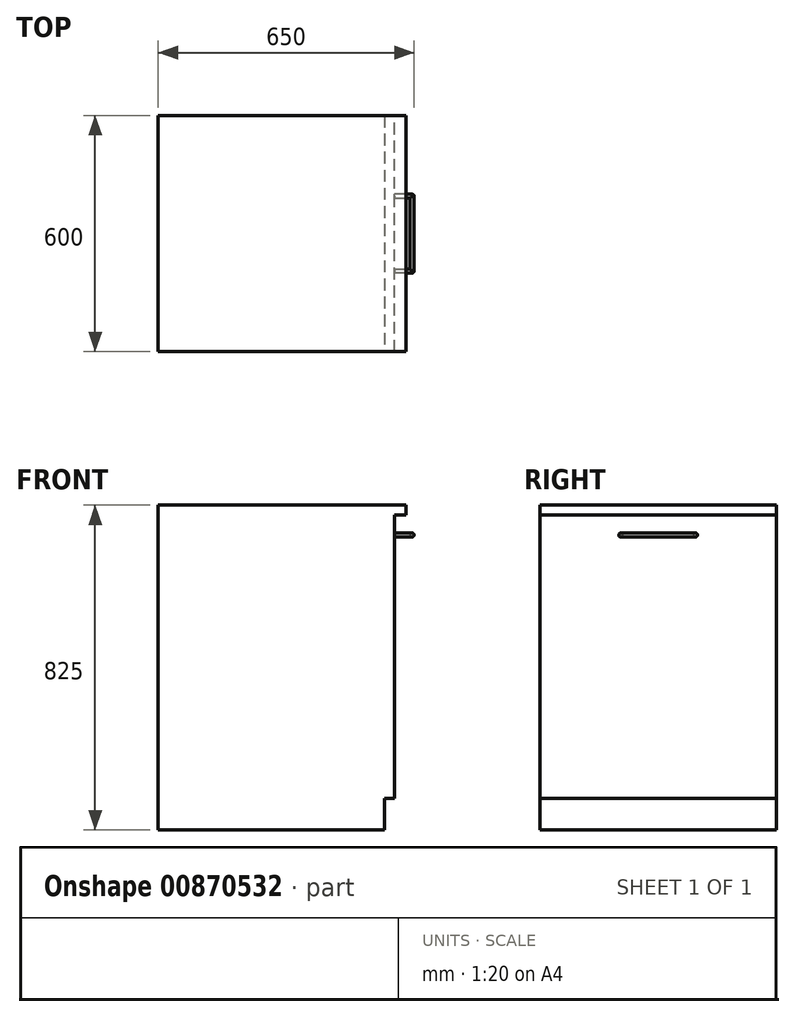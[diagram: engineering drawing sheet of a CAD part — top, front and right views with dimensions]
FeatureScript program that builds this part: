
annotation { "Feature Type Name" : "Feature", "Feature Type Description" : "" }
export const myFeature = defineFeature(function(context is Context, id is Id, definition is map)
    precondition{}
    {
        {
            var Q0;
            Q0=qCreatedBy(makeId("Top.planeOp"),FACE);
            var sketch = newSketch(context, id + "F0", { "sketchPlane" : qUnion([Q0])});
            skLineSegment(sketch, "E0.bottom", {"start": v(-300, 300) * mm, "end": v(300, 300) * mm});
            skLineSegment(sketch, "E0.top", {"start": v(-300, -300) * mm, "end": v(300, -300) * mm});
            skLineSegment(sketch, "E0.left", {"start": v(-300, 300) * mm, "end": v(-300, -300) * mm});
            skLineSegment(sketch, "E0.right", {"start": v(300, 300) * mm, "end": v(300, -300) * mm});
            skPoint(sketch, "E0.middle", {"position": v(0, 0) * mm});
            skSolve(sketch);
        }
        {
            var Q0;
            Q0=qSketchRegion(id+"F0",true);
            extrude(context, id + "F1", {"entities" : qUnion([Q0]), "depth" : 800 * mm, "offsetDistance" : 25 * mm});
        }
        {
            var Q0;
            Q0=makeQuery(id+"F1.opExtrude","SWEPT_FACE",FACE,{"disambiguationData":[OSD([sQuery(id+"F0.wireOp",EDGE,"E0.right")])]});
            var sketch = newSketch(context, id + "F2", { "sketchPlane" : qUnion([Q0])});
            skLineSegment(sketch, "E1.bottom", {"start": v(-300, 0) * mm, "end": v(300, 0) * mm});
            skLineSegment(sketch, "E1.top", {"start": v(-300, 80) * mm, "end": v(300, 80) * mm});
            skLineSegment(sketch, "E1.left", {"start": v(-300, 0) * mm, "end": v(-300, 80) * mm});
            skLineSegment(sketch, "E1.right", {"start": v(300, 0) * mm, "end": v(300, 80) * mm});
            skSolve(sketch);
        }
        {
            var Q0;
            Q0=qSketchRegion(id+"F2",true);
            extrude(context, id + "F3", {"entities" : qUnion([Q0]), "operationType" : NewBodyOperationType.REMOVE, "oppositeDirection" : true, "depth" : 25 * mm, "offsetDistance" : 25 * mm});
        }
        {
            var Q0;
            Q0=makeQuery(id+"F1.opExtrude","CAP_FACE",FACE,{"disambiguationData":[OSD([sQuery(id+"F0.wireOp",EDGE,"E0.bottom"),sQuery(id+"F0.wireOp",EDGE,"E0.top"),sQuery(id+"F0.wireOp",EDGE,"E0.left"),sQuery(id+"F0.wireOp",EDGE,"E0.right")])],"isStart":false});
            var sketch = newSketch(context, id + "F4", { "sketchPlane" : qUnion([Q0])});
            skLineSegment(sketch, "E2.bottom", {"start": v(-300, -300) * mm, "end": v(330, -300) * mm});
            skLineSegment(sketch, "E2.top", {"start": v(-300, 300) * mm, "end": v(330, 300) * mm});
            skLineSegment(sketch, "E2.left", {"start": v(-300, -300) * mm, "end": v(-300, 300) * mm});
            skLineSegment(sketch, "E2.right", {"start": v(330, -300) * mm, "end": v(330, 300) * mm});
            skSolve(sketch);
        }
        {
            var Q0;
            Q0=qSketchRegion(id+"F4",true);
            extrude(context, id + "F5", {"entities" : qUnion([Q0]), "operationType" : NewBodyOperationType.ADD, "depth" : 25 * mm, "offsetDistance" : 25 * mm});
        }
        {
            var Q0;
            Q0=makeQuery(id+"F1.opExtrude","SWEPT_FACE",FACE,{"disambiguationData":[OSD([sQuery(id+"F0.wireOp",EDGE,"E0.right")])]});
            var sketch = newSketch(context, id + "F6", { "sketchPlane" : qUnion([Q0])});
            skLineSegment(sketch, "E3.bottom", {"start": v(95, 754.24) * mm, "end": v(-95, 754.24) * mm});
            skLineSegment(sketch, "E3.top", {"start": v(95, 744.24) * mm, "end": v(-95, 744.24) * mm});
            skLineSegment(sketch, "E3.left", {"start": v(100, 749.24) * mm, "end": v(100, 749.24) * mm});
            skLineSegment(sketch, "E3.right", {"start": v(-100, 749.24) * mm, "end": v(-100, 749.24) * mm});
            skPoint(sketch, "E3.middle", {"position": v(0, 749.24) * mm});
            skPoint(sketch, "E3.middle.positionSnap0", {"position": v(0, 80) * mm});
            skPoint(sketch, "E3.centerSnap0", {"position": v(0, 80) * mm});
            skPoint(sketch, "E4.visualSharp", {"position": v(100, 744.24) * mm});
            skArc(sketch, "E4.filletArc", {"start": v(95, 744.24) * mm, "mid": v(98.54, 745.7) * mm, "end": v(100, 749.24) * mm});
            skPoint(sketch, "E5.visualSharp", {"position": v(100, 754.24) * mm});
            skArc(sketch, "E5.filletArc", {"start": v(100, 749.24) * mm, "mid": v(98.54, 752.78) * mm, "end": v(95, 754.24) * mm});
            skPoint(sketch, "E6.visualSharp", {"position": v(-100, 754.24) * mm});
            skArc(sketch, "E6.filletArc", {"start": v(-95, 754.24) * mm, "mid": v(-98.54, 752.78) * mm, "end": v(-100, 749.24) * mm});
            skPoint(sketch, "E7.visualSharp", {"position": v(-100, 744.24) * mm});
            skArc(sketch, "E7.filletArc", {"start": v(-100, 749.24) * mm, "mid": v(-98.54, 745.7) * mm, "end": v(-95, 744.24) * mm});
            skSolve(sketch);
        }
        {
            var Q0;
            Q0 = qSketchRegion(id + "F6", true);
            extrude(context, id + "F7", {"entities" : qUnion([Q0]), "operationType" : NewBodyOperationType.ADD, "depth" : 50 * mm, "offsetDistance" : 25 * mm});
        }
        {
            var Q0;
            Q0=makeQuery(id+"F7.opExtrude","SWEPT_FACE",FACE,{"disambiguationData":[OSD([sQuery(id+"F6.wireOp",EDGE,"E3.top")])]});
            var sketch = newSketch(context, id + "F8", { "sketchPlane" : qUnion([Q0])});
            skLineSegment(sketch, "E8.bottom", {"start": v(300, 90) * mm, "end": v(340, 90) * mm});
            skLineSegment(sketch, "E8.top", {"start": v(300, -90) * mm, "end": v(340, -90) * mm});
            skLineSegment(sketch, "E8.left", {"start": v(300, 90) * mm, "end": v(300, -90) * mm});
            skLineSegment(sketch, "E8.right", {"start": v(340, 90) * mm, "end": v(340, -90) * mm});
            skSolve(sketch);
        }
        {
            var Q0;
            Q0 = qSketchRegion(id + "F8", true);
            extrude(context, id + "F9", {"entities" : qUnion([Q0]), "operationType" : NewBodyOperationType.REMOVE, "oppositeDirection" : true, "depth" : 25 * mm, "offsetDistance" : 25 * mm});
        }
        {
            var Q0;
            Q0=makeQuery(id+"F7.opExtrude","CAP_EDGE",EDGE,{"disambiguationData":[OSD([sQuery(id+"F6.wireOp",EDGE,"E4.filletArc"),sQuery(id+"F6.wireOp",EDGE,"E5.filletArc")])],"isStart":false});
            var Q1;
            Q1=makeQuery(id+"F7.opExtrude","CAP_EDGE",EDGE,{"disambiguationData":[OSD([sQuery(id+"F6.wireOp",EDGE,"E3.bottom")])],"isStart":false});
            var Q2;
            Q2=makeQuery(id+"F7.opExtrude","CAP_EDGE",EDGE,{"disambiguationData":[OSD([sQuery(id+"F6.wireOp",EDGE,"E3.top")])],"isStart":false});
            var Q3;
            Q3=makeQuery(id+"F9.boolean.opBoolean","COPY",EDGE,{"derivedFrom":makeQuery(id+"F9.opExtrude","CAP_EDGE",EDGE,{"disambiguationData":[OSD([sQuery(id+"F8.wireOp",EDGE,"E8.top")])],"isStart":true})});
            var Q4;
            Q4=makeQuery(id+"F9.boolean.opBoolean","COPY",EDGE,{"derivedFrom":makeQuery(id+"F9.opExtrude","CAP_EDGE",EDGE,{"disambiguationData":[OSD([sQuery(id+"F8.wireOp",EDGE,"E8.right")])],"isStart":true})});
            var Q5;
            Q5=makeQuery(id+"F9.boolean.opBoolean","COPY",EDGE,{"derivedFrom":makeQuery(id+"F9.opExtrude","CAP_EDGE",EDGE,{"disambiguationData":[OSD([sQuery(id+"F8.wireOp",EDGE,"E8.bottom")])],"isStart":true})});
            var Q6;
            Q6=makeQuery(id+"F9.boolean.opBoolean","INTERSECT",EDGE,{"derivedFrom":[makeQuery(id+"F7.opExtrude","SWEPT_FACE",FACE,{"disambiguationData":[OSD([sQuery(id+"F6.wireOp",EDGE,"E3.bottom")])]}),makeQuery(id+"F9.opExtrude","SWEPT_FACE",FACE,{"disambiguationData":[OSD([sQuery(id+"F8.wireOp",EDGE,"E8.top")])]})]});
            var Q7;
            Q7=makeQuery(id+"F9.boolean.opBoolean","INTERSECT",EDGE,{"derivedFrom":[makeQuery(id+"F7.opExtrude","SWEPT_FACE",FACE,{"disambiguationData":[OSD([sQuery(id+"F6.wireOp",EDGE,"E3.bottom")])]}),makeQuery(id+"F9.opExtrude","SWEPT_FACE",FACE,{"disambiguationData":[OSD([sQuery(id+"F8.wireOp",EDGE,"E8.right")])]})]});
            var Q8;
            Q8=makeQuery(id+"F9.boolean.opBoolean","INTERSECT",EDGE,{"derivedFrom":[makeQuery(id+"F7.opExtrude","SWEPT_FACE",FACE,{"disambiguationData":[OSD([sQuery(id+"F6.wireOp",EDGE,"E3.bottom")])]}),makeQuery(id+"F9.opExtrude","SWEPT_FACE",FACE,{"disambiguationData":[OSD([sQuery(id+"F8.wireOp",EDGE,"E8.bottom")])]})]});
            var Q9;
            Q9=makeQuery(id+"F7.opExtrude","CAP_EDGE",EDGE,{"disambiguationData":[OSD([sQuery(id+"F6.wireOp",EDGE,"E6.filletArc"),sQuery(id+"F6.wireOp",EDGE,"E7.filletArc")])],"isStart":false});
            fillet(context, id + "F10", {"entities" : qUnion([Q0, Q1, Q2, Q3, Q4, Q5, Q6, Q7, Q8, Q9]), "radius" : 5 * mm, "tangentPropagation" : true, "allowEdgeOverflow" : false});
        }
    });
